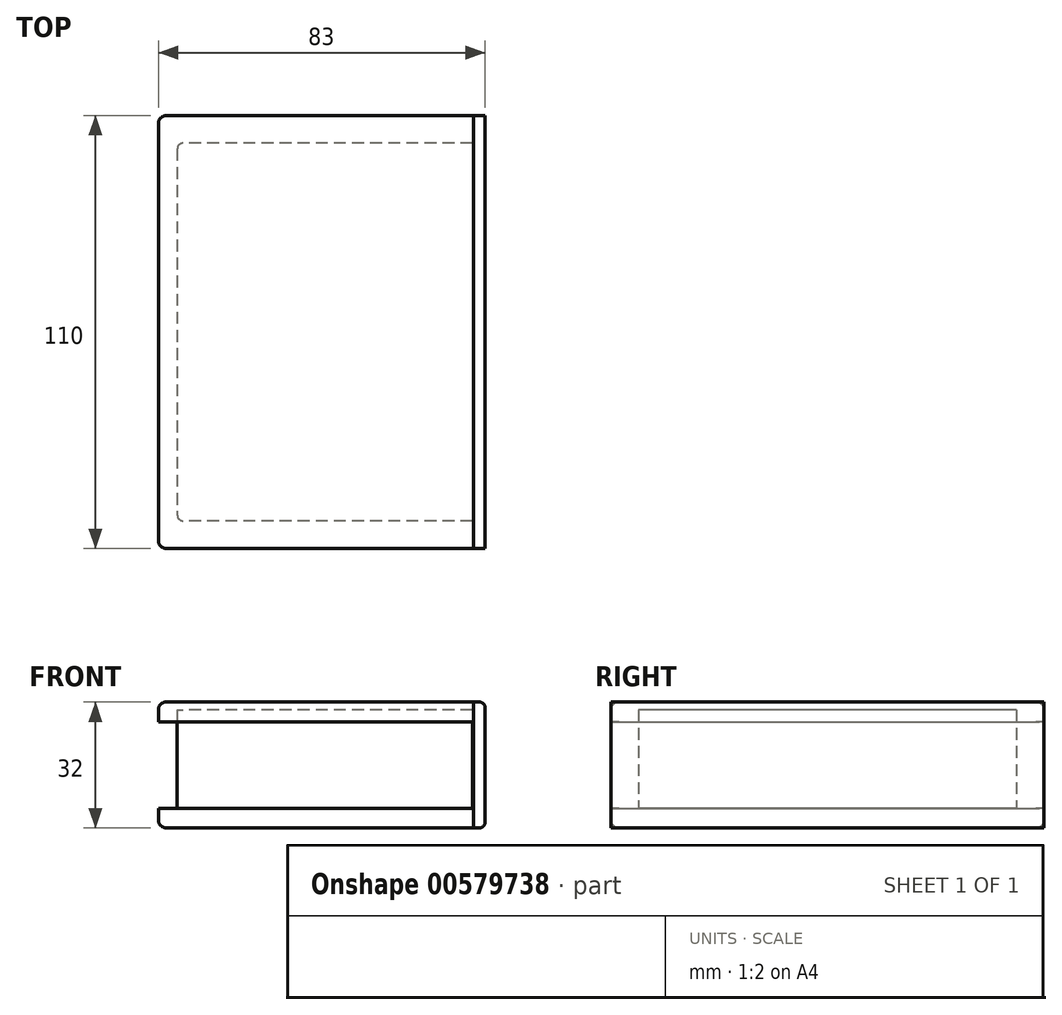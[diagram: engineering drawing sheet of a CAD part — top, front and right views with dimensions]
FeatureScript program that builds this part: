
annotation { "Feature Type Name" : "Feature", "Feature Type Description" : "" }
export const myFeature = defineFeature(function(context is Context, id is Id, definition is map)
    precondition{}
    {
        {
            var Q0;
            Q0=qCreatedBy(makeId("Top.planeOp"),FACE);
            var sketch = newSketch(context, id + "F0", { "sketchPlane" : qUnion([Q0])});
            skLineSegment(sketch, "E0.bottom", {"start": v(40, -55) * mm, "end": v(-40, -55) * mm});
            skLineSegment(sketch, "E0.top", {"start": v(40, 55) * mm, "end": v(-40, 55) * mm});
            skLineSegment(sketch, "E0.left", {"start": v(40, -55) * mm, "end": v(40, 55) * mm});
            skLineSegment(sketch, "E0.right", {"start": v(-40, -55) * mm, "end": v(-40, 55) * mm});
            skPoint(sketch, "E0.middle", {"position": v(0, 0) * mm});
            skLineSegment(sketch, "E1", {"start": v(40, 48) * mm, "end": v(40, -48) * mm});
            skSolve(sketch);
        }
        {
            var Q0;
            Q0=qCreatedBy(makeId("Top.planeOp"),FACE);
            cPlane(context, id + "F1", {"entities" : qUnion([Q0]), "cplaneType" : CPlaneType.OFFSET, "offset" : 5 * mm, "width" : 150 * mm, "height" : 150 * mm});
        }
        {
            var Q0;
            Q0=qCreatedBy(id+"F1.planeOp",FACE);
            cPlane(context, id + "F2", {"entities" : qUnion([Q0]), "cplaneType" : CPlaneType.OFFSET, "offset" : 22 * mm, "width" : 150 * mm, "height" : 150 * mm});
        }
        {
            var Q0;
            Q0=qCreatedBy(id+"F2.planeOp",FACE);
            var sketch = newSketch(context, id + "F3", { "sketchPlane" : qUnion([Q0])});
            skLineSegment(sketch, "E2.bottom", {"start": v(40, -55) * mm, "end": v(-40, -55) * mm});
            skLineSegment(sketch, "E2.top", {"start": v(40, 55) * mm, "end": v(-40, 55) * mm});
            skLineSegment(sketch, "E2.left", {"start": v(40, -55) * mm, "end": v(40, 55) * mm});
            skLineSegment(sketch, "E2.right", {"start": v(-40, -55) * mm, "end": v(-40, 55) * mm});
            skPoint(sketch, "E2.middle", {"position": v(0, 0) * mm});
            skSolve(sketch);
        }
        {
            var Q0;
            Q0=makeQuery(id+"F0.imprint","IMPRINT",FACE,{"disambiguationData":[TD([[makeQuery(id+"F0.imprint","IMPRINT",EDGE,{"derivedFrom":sQuery(id+"F0.wireOp",EDGE,"E0.bottom")}),-1.0]])]});
            var Q1;
            Q1=makeQuery(id+"F3.imprint","IMPRINT",FACE,{"disambiguationData":[TD([[makeQuery(id+"F3.imprint","IMPRINT",EDGE,{"derivedFrom":sQuery(id+"F3.wireOp",EDGE,"E2.bottom")}),-1.0]])]});
            extrude(context, id + "F4", {"entities" : qUnion([Q0, Q1]), "depth" : 5 * mm, "offsetDistance" : 25 * mm});
        }
        {
            var Q0;
            Q0=qCreatedBy(makeId("Right.planeOp"),FACE);
            cPlane(context, id + "F5", {"entities" : qUnion([Q0]), "cplaneType" : CPlaneType.OFFSET, "offset" : 40 * mm, "width" : 150 * mm, "height" : 150 * mm});
        }
        {
            var Q0;
            Q0=qCreatedBy(id+"F5.planeOp",FACE);
            var sketch = newSketch(context, id + "F6", { "sketchPlane" : qUnion([Q0])});
            skLineSegment(sketch, "E3.bottom", {"start": v(-55, 0) * mm, "end": v(55, 0) * mm});
            skLineSegment(sketch, "E3.top", {"start": v(-55, 32) * mm, "end": v(55, 32) * mm});
            skLineSegment(sketch, "E3.left", {"start": v(-55, 0) * mm, "end": v(-55, 32) * mm});
            skLineSegment(sketch, "E3.right", {"start": v(55, 0) * mm, "end": v(55, 32) * mm});
            skSolve(sketch);
        }
        {
            var Q0;
            Q0=makeQuery(id+"F6.imprint","IMPRINT",FACE,{"disambiguationData":[TD([[makeQuery(id+"F6.imprint","IMPRINT",EDGE,{"derivedFrom":sQuery(id+"F6.wireOp",EDGE,"E3.bottom")}),1.0]])]});
            extrude(context, id + "F7", {"entities" : qUnion([Q0]), "depth" : 3 * mm, "offsetDistance" : 25 * mm});
        }
        {
            var Q0;
            Q0=makeQuery(id+"F4.opExtrude","CAP_EDGE",EDGE,{"disambiguationData":[OSD([sQuery(id+"F3.wireOp",EDGE,"E2.top")])],"isStart":false});
            var Q1;
            Q1=makeQuery(id+"F4.opExtrude","CAP_EDGE",EDGE,{"disambiguationData":[OSD([sQuery(id+"F3.wireOp",EDGE,"E2.bottom")])],"isStart":false});
            var Q2;
            Q2=makeQuery(id+"F4.opExtrude","CAP_EDGE",EDGE,{"disambiguationData":[OSD([sQuery(id+"F3.wireOp",EDGE,"E2.right")])],"isStart":false});
            var Q3;
            Q3=makeQuery(id+"F4.opExtrude","SWEPT_EDGE",EDGE,{"disambiguationData":[OSD([sQuery(id+"F3.wireOp",EDGE,"E2.top"),sQuery(id+"F3.wireOp",EDGE,"E2.right")])]});
            var Q4;
            Q4=makeQuery(id+"F4.opExtrude","SWEPT_EDGE",EDGE,{"disambiguationData":[OSD([sQuery(id+"F3.wireOp",EDGE,"E2.bottom"),sQuery(id+"F3.wireOp",EDGE,"E2.right")])]});
            var Q5;
            Q5=makeQuery(id+"F4.opExtrude","SWEPT_EDGE",EDGE,{"disambiguationData":[OSD([sQuery(id+"F0.wireOp",EDGE,"E0.top"),sQuery(id+"F0.wireOp",EDGE,"E0.right")])]});
            var Q6;
            Q6=makeQuery(id+"F4.opExtrude","SWEPT_EDGE",EDGE,{"disambiguationData":[OSD([sQuery(id+"F0.wireOp",EDGE,"E0.bottom"),sQuery(id+"F0.wireOp",EDGE,"E0.right")])]});
            var Q7;
            Q7=makeQuery(id+"F4.opExtrude","CAP_EDGE",EDGE,{"disambiguationData":[OSD([sQuery(id+"F0.wireOp",EDGE,"E0.right")])],"isStart":true});
            var Q8;
            Q8=makeQuery(id+"F4.opExtrude","CAP_EDGE",EDGE,{"disambiguationData":[OSD([sQuery(id+"F0.wireOp",EDGE,"E0.top")])],"isStart":true});
            var Q9;
            Q9=makeQuery(id+"F4.opExtrude","CAP_EDGE",EDGE,{"disambiguationData":[OSD([sQuery(id+"F0.wireOp",EDGE,"E0.bottom")])],"isStart":true});
            fillet(context, id + "F8", {"entities" : qUnion([Q0, Q1, Q2, Q3, Q4, Q5, Q6, Q7, Q8, Q9]), "radius" : 2 * mm, "tangentPropagation" : true, "allowEdgeOverflow" : false});
        }
        {
            var Q0;
            Q0=makeQuery(id+"F7.opExtrude","CAP_EDGE",EDGE,{"disambiguationData":[OSD([sQuery(id+"F6.wireOp",EDGE,"E3.bottom")])],"isStart":false});
            var Q1;
            Q1=makeQuery(id+"F7.opExtrude","CAP_EDGE",EDGE,{"disambiguationData":[OSD([sQuery(id+"F6.wireOp",EDGE,"E3.top")])],"isStart":false});
            fillet(context, id + "F9", {"entities" : qUnion([Q0, Q1]), "radius" : 1.5 * mm, "tangentPropagation" : true, "allowEdgeOverflow" : false});
        }
        {
            var Q0;
            Q0=qCreatedBy(makeId("Top.planeOp"),FACE);
            cPlane(context, id + "F10", {"entities" : qUnion([Q0]), "cplaneType" : CPlaneType.OFFSET, "offset" : 5 * mm, "width" : 150 * mm, "height" : 150 * mm});
        }
        {
            var Q0;
            Q0=qCreatedBy(id+"F10.planeOp",FACE);
            var sketch = newSketch(context, id + "F11", { "sketchPlane" : qUnion([Q0])});
            skLineSegment(sketch, "E4.bottom", {"start": v(39.81, 48) * mm, "end": v(-35.19, 48) * mm});
            skLineSegment(sketch, "E4.top", {"start": v(39.81, -48) * mm, "end": v(-35.19, -48) * mm});
            skLineSegment(sketch, "E4.left", {"start": v(39.81, 48) * mm, "end": v(39.81, -48) * mm});
            skLineSegment(sketch, "E4.right", {"start": v(-35.19, 48) * mm, "end": v(-35.19, -48) * mm});
            skSolve(sketch);
        }
        {
            var Q0;
            Q0=makeQuery(id+"F11.imprint","IMPRINT",FACE,{"disambiguationData":[TD([[makeQuery(id+"F11.imprint","IMPRINT",EDGE,{"derivedFrom":sQuery(id+"F11.wireOp",EDGE,"E4.bottom")}),1.0]])]});
            extrude(context, id + "F12", {"entities" : qUnion([Q0]), "depth" : 25 * mm, "offsetDistance" : 25 * mm});
        }
        {
            var Q0;
            Q0=makeQuery(id+"F12.opExtrude","SWEPT_EDGE",EDGE,{"disambiguationData":[OSD([sQuery(id+"F11.wireOp",EDGE,"E4.bottom"),sQuery(id+"F11.wireOp",EDGE,"E4.right")])]});
            var Q1;
            Q1=makeQuery(id+"F12.opExtrude","SWEPT_EDGE",EDGE,{"disambiguationData":[OSD([sQuery(id+"F11.wireOp",EDGE,"E4.top"),sQuery(id+"F11.wireOp",EDGE,"E4.right")])]});
            fillet(context, id + "F13", {"entities" : qUnion([Q0, Q1]), "radius" : 1.5 * mm, "tangentPropagation" : true, "allowEdgeOverflow" : false});
        }
    });
